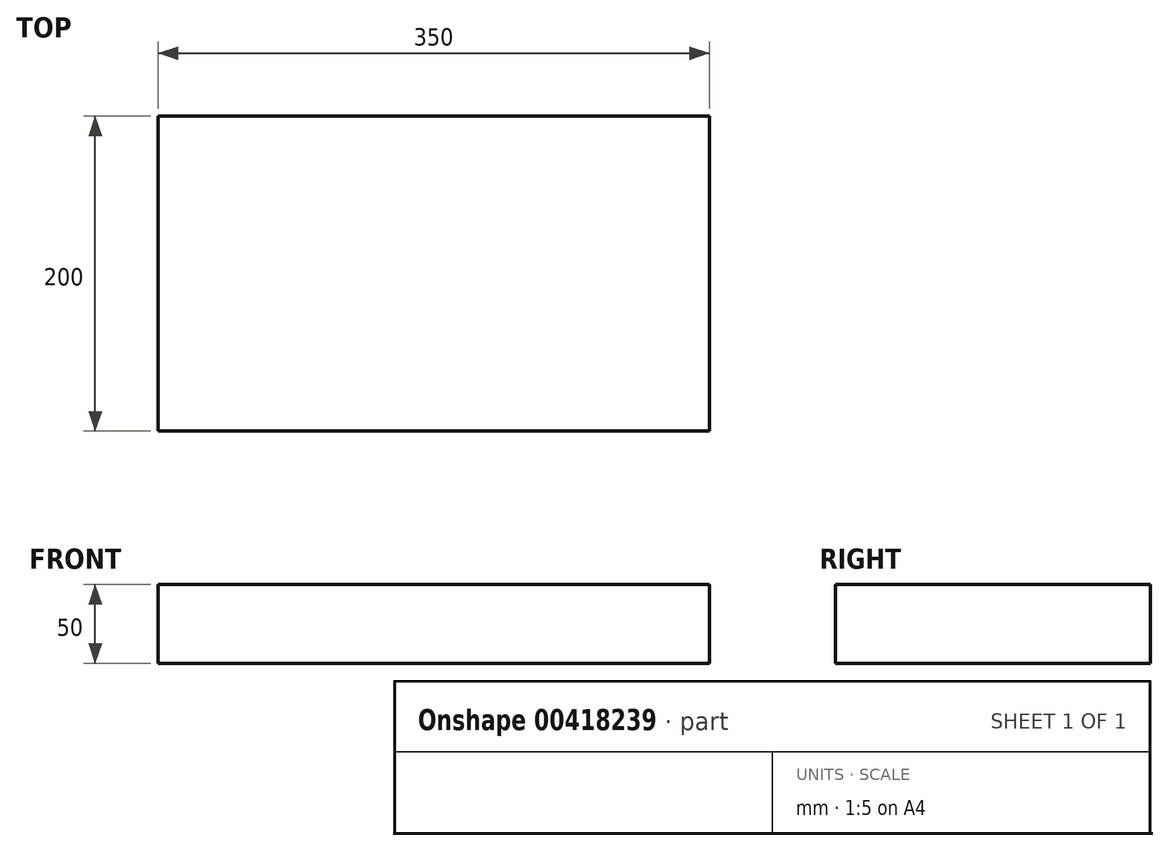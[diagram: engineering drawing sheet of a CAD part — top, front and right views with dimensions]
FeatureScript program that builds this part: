
annotation { "Feature Type Name" : "Feature", "Feature Type Description" : "" }
export const myFeature = defineFeature(function(context is Context, id is Id, definition is map)
    precondition{}
    {
        {
            var Q0;
            Q0=qCreatedBy(makeId("Top.planeOp"),FACE);
            var sketch = newSketch(context, id + "F0", { "sketchPlane" : qUnion([Q0])});
            skLineSegment(sketch, "E0.bottom", {"start": v(158.84, -18.33) * mm, "end": v(-191.16, -18.33) * mm});
            skLineSegment(sketch, "E0.top", {"start": v(158.84, -218.33) * mm, "end": v(-191.16, -218.33) * mm});
            skLineSegment(sketch, "E0.left", {"start": v(158.84, -18.33) * mm, "end": v(158.84, -218.33) * mm});
            skLineSegment(sketch, "E0.right", {"start": v(-191.16, -18.33) * mm, "end": v(-191.16, -218.33) * mm});
            skSolve(sketch);
        }
        {
            var Q0;
            Q0=makeQuery(id+"F0.imprint","IMPRINT",FACE,{"disambiguationData":[TD([[makeQuery(id+"F0.imprint","IMPRINT",EDGE,{"derivedFrom":sQuery(id+"F0.wireOp",EDGE,"E0.bottom")}),1.0]])]});
            extrude(context, id + "F1", {"entities" : qUnion([Q0]), "depth" : 50 * mm});
        }
    });
